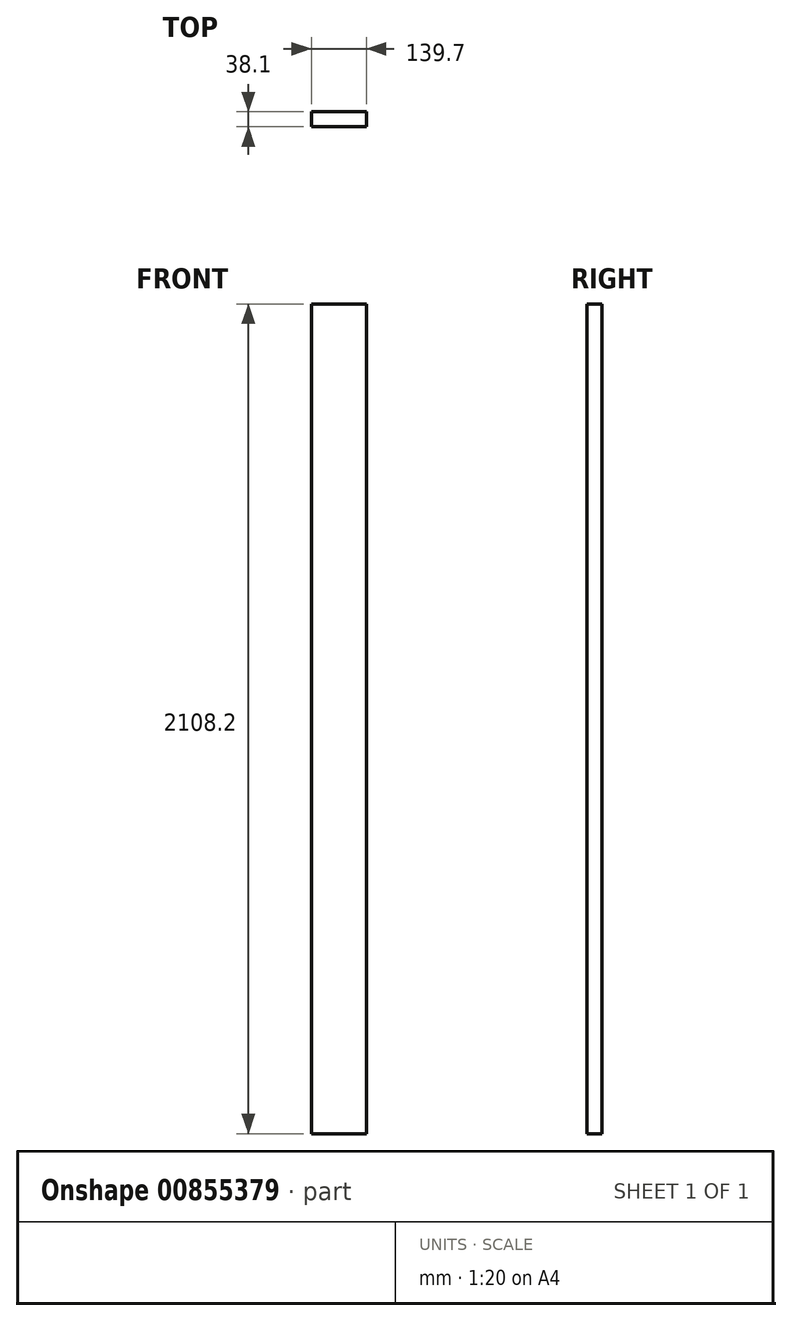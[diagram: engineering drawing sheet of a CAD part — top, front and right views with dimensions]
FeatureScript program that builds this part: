
annotation { "Feature Type Name" : "Feature", "Feature Type Description" : "" }
export const myFeature = defineFeature(function(context is Context, id is Id, definition is map)
    precondition{}
    {
        {
            var Q0;
            Q0=qCreatedBy(makeId("Top.planeOp"),FACE);
            var sketch = newSketch(context, id + "F0", { "sketchPlane" : qUnion([Q0])});
            skLineSegment(sketch, "E0.bottom", {"start": v(0, 0) * mm, "end": v(139.7, 0) * mm});
            skLineSegment(sketch, "E0.top", {"start": v(0, 38.1) * mm, "end": v(139.7, 38.1) * mm});
            skLineSegment(sketch, "E0.left", {"start": v(0, 0) * mm, "end": v(0, 38.1) * mm});
            skLineSegment(sketch, "E0.right", {"start": v(139.7, 0) * mm, "end": v(139.7, 38.1) * mm});
            skSolve(sketch);
        }
        {
            var Q0;
            Q0 = qSketchRegion(id + "F0", true);
            extrude(context, id + "F1", {"entities" : qUnion([Q0]), "depth" : 2108.2 * mm, "offsetDistance" : 25.4 * mm});
        }
    });
